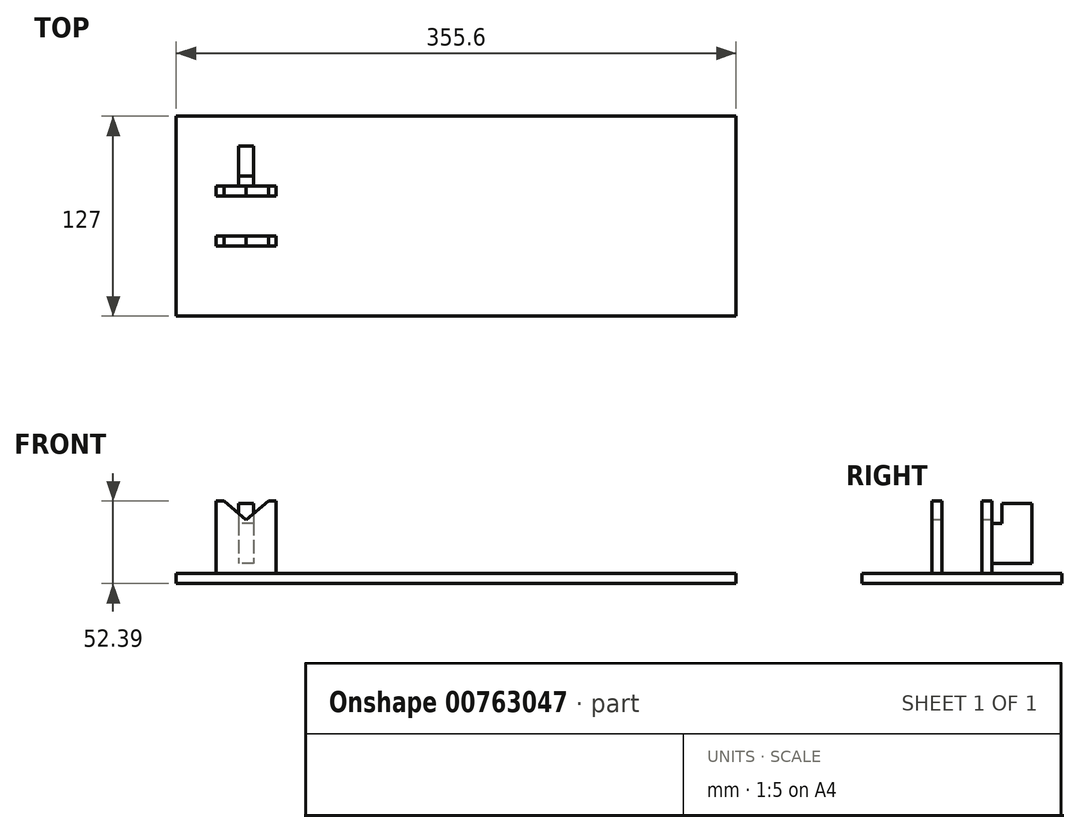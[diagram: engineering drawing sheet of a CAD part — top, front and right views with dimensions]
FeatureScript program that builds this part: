
annotation { "Feature Type Name" : "Feature", "Feature Type Description" : "" }
export const myFeature = defineFeature(function(context is Context, id is Id, definition is map)
    precondition{}
    {
        {
            var Q0;
            Q0=qCreatedBy(makeId("Top.planeOp"),FACE);
            var sketch = newSketch(context, id + "F0", { "sketchPlane" : qUnion([Q0])});
            skLineSegment(sketch, "E0.bottom", {"start": v(0, 4.6) * mm, "end": v(355.6, 4.6) * mm});
            skLineSegment(sketch, "E0.top", {"start": v(0, 131.6) * mm, "end": v(355.6, 131.6) * mm});
            skLineSegment(sketch, "E0.left", {"start": v(0, 4.6) * mm, "end": v(0, 131.6) * mm});
            skLineSegment(sketch, "E0.right", {"start": v(355.6, 4.6) * mm, "end": v(355.6, 131.6) * mm});
            skSolve(sketch);
        }
        {
            var Q0;
            Q0 = qSketchRegion(id + "F0", true);
            extrude(context, id + "F1", {"entities" : qUnion([Q0]), "depth" : 6.35 * mm, "offsetDistance" : 25.4 * mm});
        }
        {
            var Q0;
            Q0=makeQuery(id+"F1.opExtrude","CAP_FACE",FACE,{"disambiguationData":[OSD([sQuery(id+"F0.wireOp",EDGE,"E0.bottom"),sQuery(id+"F0.wireOp",EDGE,"E0.top"),sQuery(id+"F0.wireOp",EDGE,"E0.left"),sQuery(id+"F0.wireOp",EDGE,"E0.right")])],"isStart":false});
            var sketch = newSketch(context, id + "F2", { "sketchPlane" : qUnion([Q0])});
            skLineSegment(sketch, "E1.bottom", {"start": v(25.4, 49.04) * mm, "end": v(63.5, 49.04) * mm});
            skLineSegment(sketch, "E1.top", {"start": v(25.4, 55.4) * mm, "end": v(63.5, 55.4) * mm});
            skLineSegment(sketch, "E1.left", {"start": v(25.4, 49.04) * mm, "end": v(25.4, 55.4) * mm});
            skLineSegment(sketch, "E1.right", {"start": v(63.5, 49.04) * mm, "end": v(63.5, 55.4) * mm});
            skLineSegment(sketch, "E2.0.1.0", {"start": v(25.4, 80.8) * mm, "end": v(63.5, 80.8) * mm});
            skLineSegment(sketch, "E2.0.1.1", {"start": v(25.4, 87.14) * mm, "end": v(63.5, 87.14) * mm});
            skLineSegment(sketch, "E2.0.1.2", {"start": v(63.5, 80.8) * mm, "end": v(63.5, 87.14) * mm});
            skLineSegment(sketch, "E2.0.1.3", {"start": v(25.4, 80.8) * mm, "end": v(25.4, 87.14) * mm});
            skLineSegment(sketch, "E2.direction1", {"start": v(25.4, 49.04) * mm, "end": v(50.8, 49.04) * mm, "construction": true});
            skLineSegment(sketch, "E2.direction2", {"start": v(25.4, 49.04) * mm, "end": v(25.4, 80.8) * mm, "construction": true});
            skSolve(sketch);
        }
        {
            var Q0;
            Q0 = qSketchRegion(id + "F2", true);
            extrude(context, id + "F3", {"entities" : qUnion([Q0]), "operationType" : NewBodyOperationType.ADD, "depth" : 50.8 * mm, "offsetDistance" : 25.4 * mm});
        }
        {
            var Q0;
            Q0=makeQuery(id+"F3.opExtrude","SWEPT_FACE",FACE,{"disambiguationData":[OSD([sQuery(id+"F2.wireOp",EDGE,"E1.bottom")])]});
            var sketch = newSketch(context, id + "F4", { "sketchPlane" : qUnion([Q0])});
            skCircle(sketch, "E3", {"center": v(44.45, 57.15) * mm, "radius": 12.7 * mm, "construction": true});
            skLineSegment(sketch, "E4", {"start": v(25.4, 57.15) * mm, "end": v(63.5, 57.15) * mm});
            skLineSegment(sketch, "E5.0", {"start": v(25.4, 52.39) * mm, "end": v(30.37, 52.39) * mm});
            skLineSegment(sketch, "E6", {"start": v(25.4, 57.15) * mm, "end": v(25.4, 52.39) * mm});
            skLineSegment(sketch, "E7", {"start": v(63.5, 57.15) * mm, "end": v(63.5, 52.39) * mm});
            skLineSegment(sketch, "E8.trimOffspring", {"start": v(58.53, 52.39) * mm, "end": v(63.5, 52.39) * mm});
            skPoint(sketch, "E9.orphan", {"position": v(44.45, 39.19) * mm});
            skLineSegment(sketch, "E10.0", {"start": v(30.37, 52.39) * mm, "end": v(44.45, 40.57) * mm});
            skLineSegment(sketch, "E11.0", {"start": v(58.53, 52.39) * mm, "end": v(44.45, 40.57) * mm});
            skLineSegment(sketch, "E12", {"start": v(36.29, 47.42) * mm, "end": v(44.45, 57.15) * mm, "construction": true});
            skLineSegment(sketch, "E13", {"start": v(52.61, 47.42) * mm, "end": v(44.45, 57.15) * mm, "construction": true});
            skSolve(sketch);
        }
        {
            var Q0;
            Q0 = qSketchRegion(id + "F4", true);
            var Q1;
            Q1=makeQuery(id+"F3.opExtrude","SWEPT_FACE",FACE,{"disambiguationData":[OSD([sQuery(id+"F2.wireOp",EDGE,"E2.0.1.1")])]});
            extrude(context, id + "F5", {"entities" : qUnion([Q0, Q1]), "operationType" : NewBodyOperationType.REMOVE, "oppositeDirection" : true, "depth" : 50.8 * mm, "offsetDistance" : 25.4 * mm});
        }
        {
            var Q0;
            Q0=makeQuery(id+"F3.opExtrude","SWEPT_FACE",FACE,{"disambiguationData":[OSD([sQuery(id+"F2.wireOp",EDGE,"E2.0.1.1")])]});
            var sketch = newSketch(context, id + "F6", { "sketchPlane" : qUnion([Q0])});
            skLineSegment(sketch, "E14.bottom", {"start": v(-49.21, 38.1) * mm, "end": v(-39.69, 38.1) * mm});
            skLineSegment(sketch, "E14.top", {"start": v(-49.21, 12.7) * mm, "end": v(-39.69, 12.7) * mm});
            skLineSegment(sketch, "E14.left", {"start": v(-49.21, 38.1) * mm, "end": v(-49.21, 12.7) * mm});
            skLineSegment(sketch, "E14.right", {"start": v(-39.69, 38.1) * mm, "end": v(-39.69, 12.7) * mm});
            skSolve(sketch);
        }
        {
            var Q0;
            Q0 = qSketchRegion(id + "F6", true);
            extrude(context, id + "F7", {"entities" : qUnion([Q0]), "operationType" : NewBodyOperationType.ADD, "depth" : 25.4 * mm, "offsetDistance" : 25.4 * mm});
        }
        {
            var Q0;
            Q0=makeQuery(id+"F7.opExtrude","SWEPT_FACE",FACE,{"disambiguationData":[OSD([sQuery(id+"F6.wireOp",EDGE,"E14.bottom")])]});
            var sketch = newSketch(context, id + "F8", { "sketchPlane" : qUnion([Q0])});
            skLineSegment(sketch, "E15.bottom", {"start": v(49.21, 112.54) * mm, "end": v(39.69, 112.54) * mm});
            skLineSegment(sketch, "E15.top", {"start": v(49.21, 93.5) * mm, "end": v(39.69, 93.5) * mm});
            skLineSegment(sketch, "E15.left", {"start": v(49.21, 112.54) * mm, "end": v(49.21, 93.5) * mm});
            skLineSegment(sketch, "E15.right", {"start": v(39.69, 112.54) * mm, "end": v(39.69, 93.5) * mm});
            skSolve(sketch);
        }
        {
            var Q0;
            Q0 = qSketchRegion(id + "F8", true);
            extrude(context, id + "F9", {"entities" : qUnion([Q0]), "operationType" : NewBodyOperationType.ADD, "depth" : 12.7 * mm, "offsetDistance" : 25.4 * mm});
        }
    });
